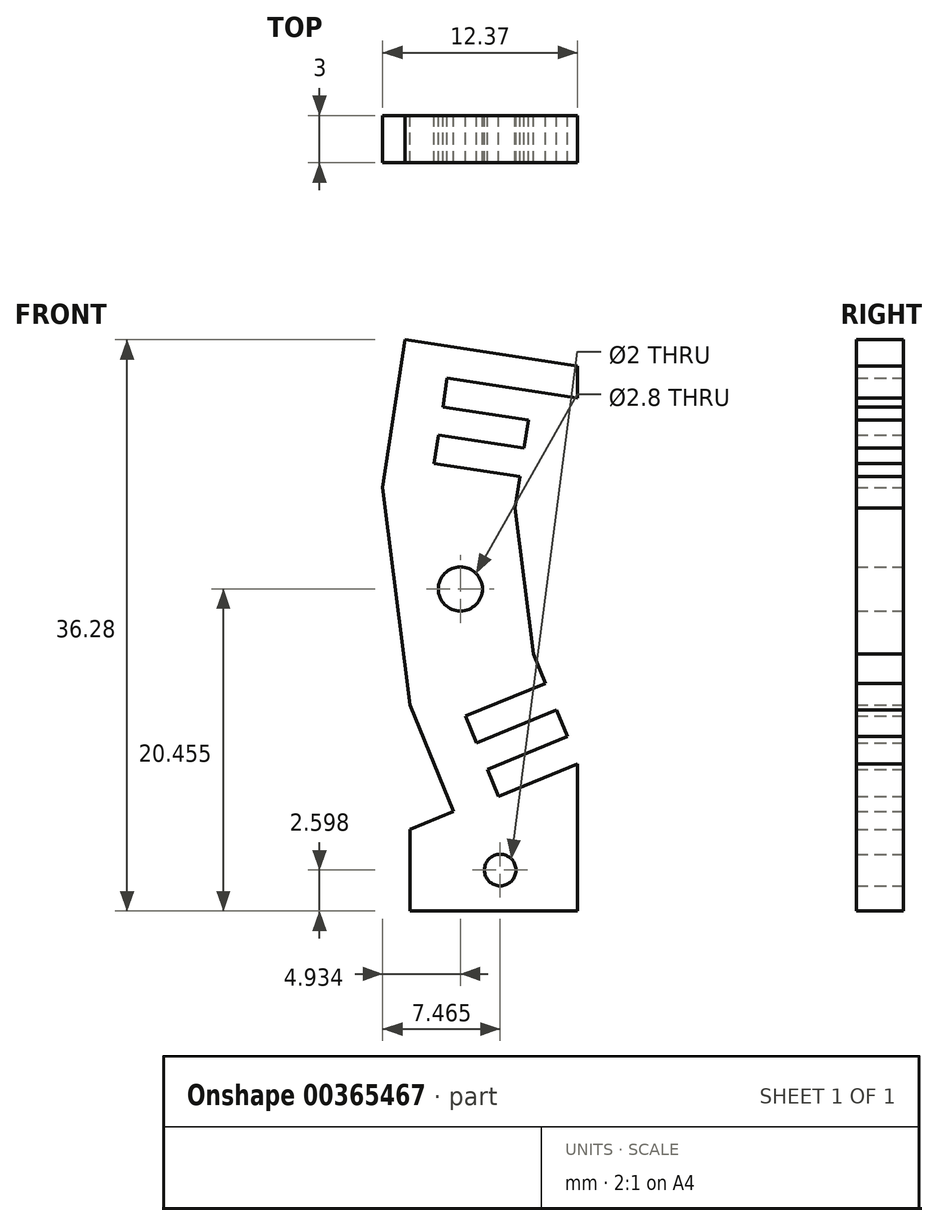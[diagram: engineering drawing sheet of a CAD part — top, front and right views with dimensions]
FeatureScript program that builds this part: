
annotation { "Feature Type Name" : "Feature", "Feature Type Description" : "" }
export const myFeature = defineFeature(function(context is Context, id is Id, definition is map)
    precondition{}
    {
        {
            var Q0;
            Q0=qCreatedBy(makeId("Front.planeOp"),FACE);
            var sketch = newSketch(context, id + "F0", { "sketchPlane" : qUnion([Q0])});
            skLineSegment(sketch, "E0", {"start": v(62.96, -34.45) * mm, "end": v(66.2, -33.12) * mm});
            skLineSegment(sketch, "E1", {"start": v(64.11, -28.03) * mm, "end": v(60.87, -29.37) * mm});
            skLineSegment(sketch, "E2.1", {"start": v(67.35, -30.65) * mm, "end": v(66.66, -28.99) * mm});
            skLineSegment(sketch, "E2.3", {"start": v(57.34, -28.66) * mm, "end": v(60.11, -35.4) * mm});
            skLineSegment(sketch, "E3.trimOffspring", {"start": v(67.98, -41.74) * mm, "end": v(57.34, -41.74) * mm});
            skLineSegment(sketch, "E4.trimOffspring", {"start": v(57.34, -36.55) * mm, "end": v(57.34, -41.74) * mm});
            skLineSegment(sketch, "E5.trimOffspring", {"start": v(60.11, -35.4) * mm, "end": v(57.34, -36.55) * mm});
            skCircle(sketch, "E6", {"center": v(63.07, -39.14) * mm, "radius": 1 * mm});
            skPoint(sketch, "E6.centerSnap0", {"position": v(57.34, -39.14) * mm});
            skPoint(sketch, "E6.centerSnap1", {"position": v(63.07, -41.74) * mm});
            skLineSegment(sketch, "E7", {"start": v(60.95, -8.08) * mm, "end": v(59.7, -7.89) * mm});
            skLineSegment(sketch, "E8", {"start": v(58.88, -13.33) * mm, "end": v(62.34, -13.85) * mm});
            skLineSegment(sketch, "E9", {"start": v(63.17, -8.42) * mm, "end": v(60.95, -8.08) * mm});
            skLineSegment(sketch, "E10.0", {"start": v(57.04, -5.46) * mm, "end": v(55.61, -14.85) * mm});
            skLineSegment(sketch, "E10.1", {"start": v(61.25, -6.1) * mm, "end": v(57.04, -5.46) * mm});
            skLineSegment(sketch, "E10.3", {"start": v(64.02, -16.13) * mm, "end": v(64.32, -14.15) * mm});
            skLineSegment(sketch, "E10.4", {"start": v(65.45, -6.74) * mm, "end": v(61.25, -6.1) * mm});
            skLineSegment(sketch, "E11", {"start": v(55.61, -14.85) * mm, "end": v(57.34, -28.66) * mm});
            skPoint(sketch, "E12.endSnap0", {"position": v(69.62, -9.4) * mm});
            skLineSegment(sketch, "E13", {"start": v(65.45, -6.74) * mm, "end": v(67.98, -7.13) * mm});
            skPoint(sketch, "E14.orphan", {"position": v(69.62, -5.2) * mm});
            skLineSegment(sketch, "E15", {"start": v(67.98, -32.4) * mm, "end": v(67.98, -41.74) * mm});
            skPoint(sketch, "E16.orphan", {"position": v(68.81, -41.74) * mm});
            skLineSegment(sketch, "E17.trimOffspring", {"start": v(67.98, -9.15) * mm, "end": v(67.98, -7.13) * mm});
            skLineSegment(sketch, "E18", {"start": v(64.02, -16.13) * mm, "end": v(65.2, -25.42) * mm});
            skLineSegment(sketch, "E19.trimOffspring", {"start": v(65.15, -8.72) * mm, "end": v(67.98, -9.15) * mm});
            skCircle(sketch, "E20", {"center": v(60.54, -21.29) * mm, "radius": 1.4 * mm});
            skLineSegment(sketch, "E21", {"start": v(59.16, -11.5) * mm, "end": v(64.6, -12.33) * mm});
            skLineSegment(sketch, "E22", {"start": v(59.43, -9.72) * mm, "end": v(64.87, -10.55) * mm});
            skLineSegment(sketch, "E23", {"start": v(59.7, -7.89) * mm, "end": v(59.43, -9.72) * mm});
            skLineSegment(sketch, "E24", {"start": v(62.34, -13.85) * mm, "end": v(64.32, -14.15) * mm});
            skLineSegment(sketch, "E25", {"start": v(63.17, -8.42) * mm, "end": v(65.15, -8.72) * mm});
            skLineSegment(sketch, "E26.trimOffspring", {"start": v(64.6, -12.33) * mm, "end": v(64.87, -10.55) * mm});
            skPoint(sketch, "E27.orphan", {"position": v(62.76, -11.13) * mm});
            skLineSegment(sketch, "E28.trimOffspring", {"start": v(59.16, -11.5) * mm, "end": v(58.88, -13.33) * mm});
            skPoint(sketch, "E29.orphan", {"position": v(58.72, -7.74) * mm});
            skPoint(sketch, "E30.orphan", {"position": v(57.9, -13.18) * mm});
            skPoint(sketch, "E31.start.orphan", {"position": v(58.3, -10.46) * mm});
            skLineSegment(sketch, "E32", {"start": v(61.58, -31.08) * mm, "end": v(66.66, -28.99) * mm});
            skLineSegment(sketch, "E33", {"start": v(62.26, -32.74) * mm, "end": v(67.35, -30.65) * mm});
            skLineSegment(sketch, "E34", {"start": v(60.87, -29.37) * mm, "end": v(61.58, -31.08) * mm});
            skLineSegment(sketch, "E35", {"start": v(66.2, -33.12) * mm, "end": v(67.98, -32.4) * mm});
            skLineSegment(sketch, "E36", {"start": v(64.11, -28.03) * mm, "end": v(65.96, -27.27) * mm});
            skLineSegment(sketch, "E37.trimOffspring", {"start": v(65.96, -27.27) * mm, "end": v(65.2, -25.42) * mm});
            skPoint(sketch, "E38.orphan", {"position": v(59.95, -29.75) * mm});
            skPoint(sketch, "E39.orphan", {"position": v(62.04, -34.83) * mm});
            skPoint(sketch, "E40.start.orphan", {"position": v(61, -32.29) * mm});
            skLineSegment(sketch, "E41.trimOffspring", {"start": v(62.26, -32.74) * mm, "end": v(62.96, -34.45) * mm});
            skSolve(sketch);
        }
        {
            var Q0;
            Q0 = qSketchRegion(id + "F0", true);
            extrude(context, id + "F1", {"entities" : qUnion([Q0]), "depth" : 3 * mm});
        }
    });
